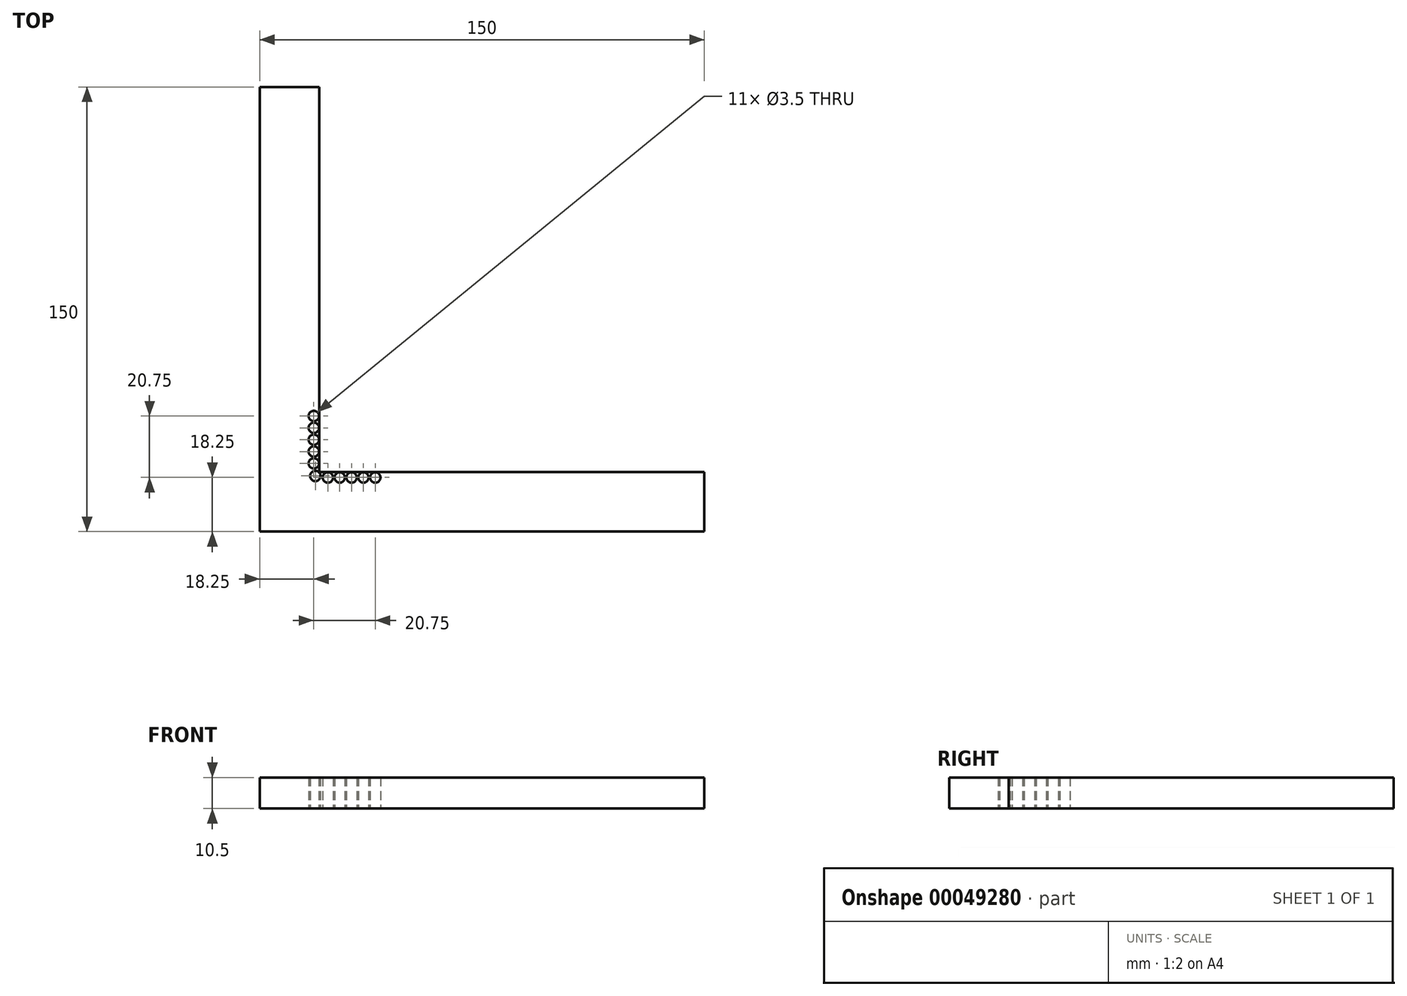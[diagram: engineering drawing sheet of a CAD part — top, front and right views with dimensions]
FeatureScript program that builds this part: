
annotation { "Feature Type Name" : "Feature", "Feature Type Description" : "" }
export const myFeature = defineFeature(function(context is Context, id is Id, definition is map)
    precondition{}
    {
        {
            var Q0;
            Q0=qCreatedBy(makeId("Top.planeOp"),FACE);
            var sketch = newSketch(context, id + "F0", { "sketchPlane" : qUnion([Q0])});
            skLineSegment(sketch, "E0.rect.bottom", {"start": v(75, -75) * mm, "end": v(-75, -75) * mm});
            skLineSegment(sketch, "E0.rect.top", {"start": v(75, 75) * mm, "end": v(-75, 75) * mm});
            skLineSegment(sketch, "E0.rect.left", {"start": v(75, -75) * mm, "end": v(75, 75) * mm});
            skLineSegment(sketch, "E0.rect.right", {"start": v(-75, -75) * mm, "end": v(-75, 75) * mm});
            skPoint(sketch, "E0.rect.middle", {"position": v(0, 0) * mm});
            skLineSegment(sketch, "E1.bottom", {"start": v(-55, -55) * mm, "end": v(75, -55) * mm, "construction": true});
            skLineSegment(sketch, "E1.top", {"start": v(-55, 75) * mm, "end": v(75, 75) * mm});
            skLineSegment(sketch, "E1.left", {"start": v(-55, -55) * mm, "end": v(-55, 75) * mm, "construction": true});
            skLineSegment(sketch, "E1.right", {"start": v(75, -55) * mm, "end": v(75, 75) * mm});
            skLineSegment(sketch, "E2", {"start": v(-55, -55) * mm, "end": v(-75, -75) * mm, "construction": true});
            skLineSegment(sketch, "E3", {"start": v(-61.67, -50.8) * mm, "end": v(-49.64, -62.83) * mm, "construction": true});
            skCircle(sketch, "E4", {"center": v(-56.24, -56.24) * mm, "radius": 1.75 * mm});
            skCircle(sketch, "E5", {"center": v(-52, -56.75) * mm, "radius": 1.75 * mm});
            skCircle(sketch, "E6.1.0.0", {"center": v(-48, -56.75) * mm, "radius": 1.75 * mm});
            skCircle(sketch, "E6.2.0.0", {"center": v(-44, -56.75) * mm, "radius": 1.75 * mm});
            skCircle(sketch, "E6.3.0.0", {"center": v(-40, -56.75) * mm, "radius": 1.75 * mm});
            skCircle(sketch, "E6.4.0.0", {"center": v(-36, -56.75) * mm, "radius": 1.75 * mm});
            skLineSegment(sketch, "E6.direction1", {"start": v(-52, -56.75) * mm, "end": v(-48, -56.75) * mm, "construction": true});
            skCircle(sketch, "E7.MirrorC", {"center": v(-56.75, -36) * mm, "radius": 1.75 * mm});
            skCircle(sketch, "E8.MirrorC", {"center": v(-56.75, -40) * mm, "radius": 1.75 * mm});
            skCircle(sketch, "E9.MirrorC", {"center": v(-56.75, -44) * mm, "radius": 1.75 * mm});
            skCircle(sketch, "E10.MirrorC", {"center": v(-56.75, -48) * mm, "radius": 1.75 * mm});
            skCircle(sketch, "E11.MirrorC", {"center": v(-56.75, -52) * mm, "radius": 1.75 * mm});
            skLineSegment(sketch, "E12.bottom", {"start": v(75, 75) * mm, "end": v(-54.9, 75) * mm});
            skLineSegment(sketch, "E12.top", {"start": v(75, -54.9) * mm, "end": v(-54.9, -54.9) * mm});
            skLineSegment(sketch, "E12.left", {"start": v(75, 75) * mm, "end": v(75, -54.9) * mm});
            skLineSegment(sketch, "E12.right", {"start": v(-54.9, 75) * mm, "end": v(-54.9, -54.9) * mm});
            skSolve(sketch);
        }
        {
            var Q0;
            Q0=makeQuery(id+"F0.imprint","IMPRINT",FACE,{"disambiguationData":[TD([[makeQuery(id+"F0.imprint","IMPRINT",EDGE,{"derivedFrom":sQuery(id+"F0.wireOp",EDGE,"E0.rect.bottom")}),-1.0]])]});
            extrude(context, id + "F1", {"entities" : qUnion([Q0]), "depth" : 10.5 * mm});
        }
    });
